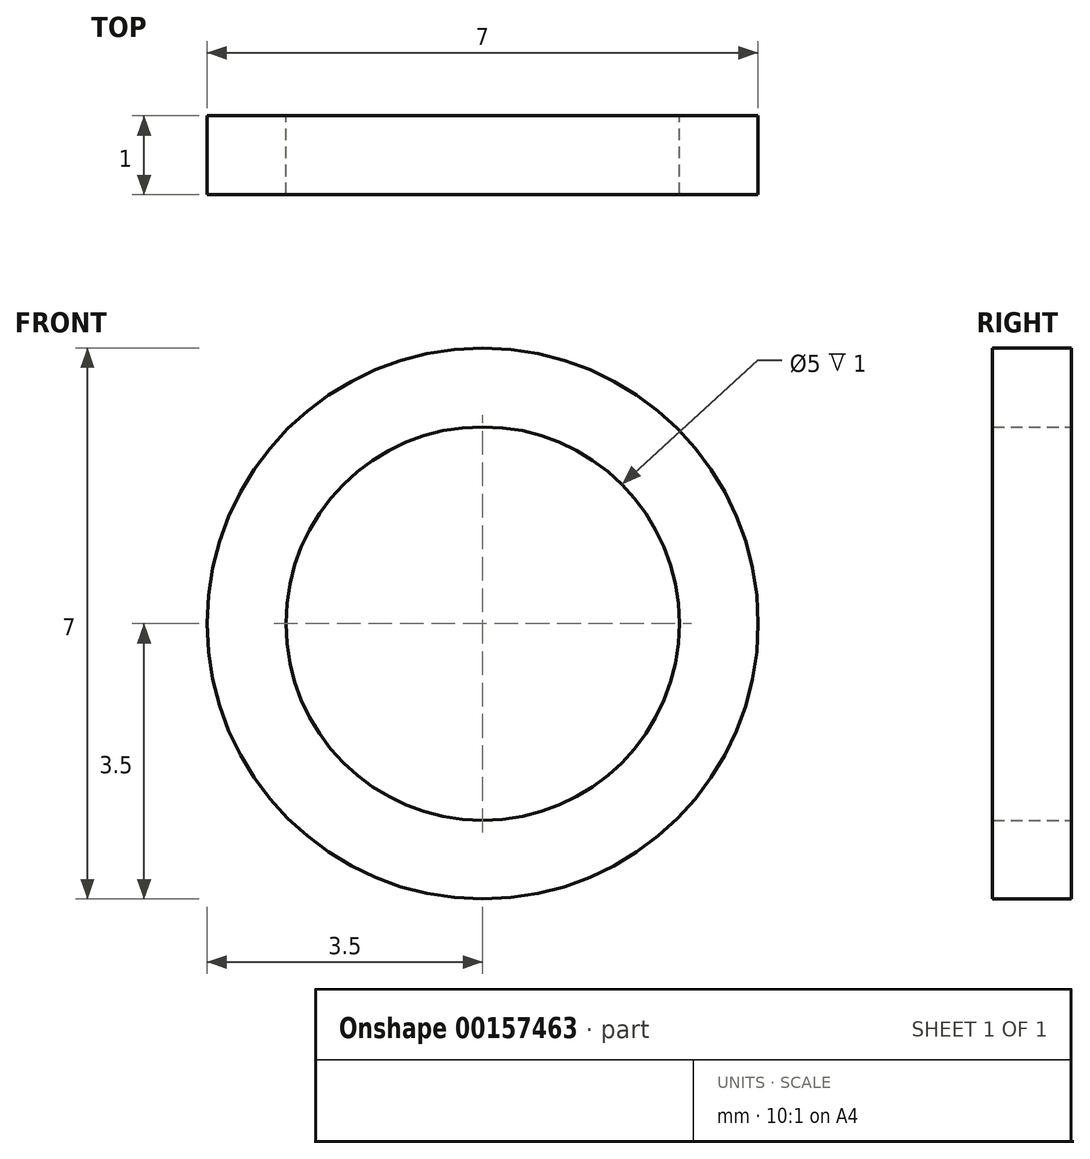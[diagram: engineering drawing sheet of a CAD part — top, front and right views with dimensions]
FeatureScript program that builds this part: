
annotation { "Feature Type Name" : "Feature", "Feature Type Description" : "" }
export const myFeature = defineFeature(function(context is Context, id is Id, definition is map)
    precondition{}
    {
        {
            var Q0;
            Q0=qCreatedBy(makeId("Front.planeOp"),FACE);
            var sketch = newSketch(context, id + "F0", { "sketchPlane" : qUnion([Q0])});
            skCircle(sketch, "E0", {"center": v(0, 0) * mm, "radius": 3.5 * mm});
            skCircle(sketch, "E1", {"center": v(0, 0) * mm, "radius": 2.5 * mm});
            skSolve(sketch);
        }
        {
            var Q0;
            Q0=makeQuery(id+"F0.imprint","IMPRINT",FACE,{"disambiguationData":[TD([[makeQuery(id+"F0.imprint","IMPRINT",EDGE,{"derivedFrom":sQuery(id+"F0.wireOp",EDGE,"E0")}),1.0]])]});
            extrude(context, id + "F1", {"entities" : qUnion([Q0]), "depth" : 1 * mm});
        }
    });
